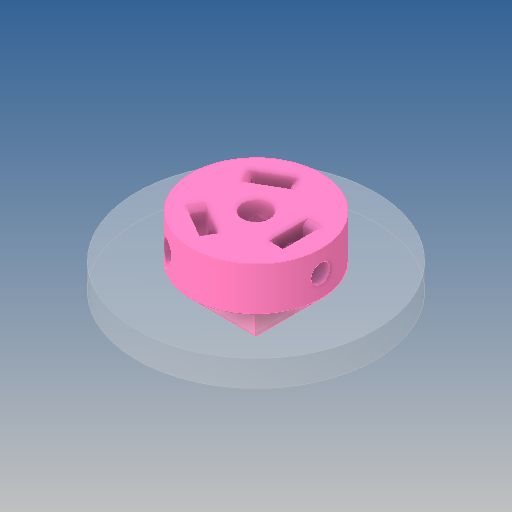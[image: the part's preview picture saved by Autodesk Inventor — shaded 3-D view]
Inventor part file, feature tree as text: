
AUTODESK INVENTOR PART (.ipt)
format: ipt  version: 2017 (Build 210142000, 142)  size: 262,656 bytes
history: native  units: mm
features: extrude x5, other x4, sketch x3, chamfer x2, pattern_circular x1, projected_geometry x1
ambient origin geometry x8: Origin, YZ Plane, XZ Plane, XY Plane, X Axis, Y Axis, Z Axis, Center Point
bodies: Body1 (feature_tree), Body2 (feature_tree)
feature tree (16):
  other  "Sólido1"
  extrude  "Extrusión1"  Depth=11.85mm
  sketch  "Boceto2"  dims[d3=6.576542mm d4=3.3mm]
  extrude  "Extrusión2"  Depth=3.3mm
  extrude  "Extrusión3"  Depth=2.0mm
  sketch  "Boceto3"  dims[d5=10.0mm d6=0.0mm d7=4.2mm d8=120.0deg d9=3.7mm d10=16.0mm d11=0.0mm d12=4.0mm d13=0.0mm d14=8.0mm d15=0.0mm d16=30.0mm d18=360.0deg d20=30.0mm d21=360.0deg d23=1.0mm d24=2.0mm d25=45.0deg d26=30.0mm d27=4.275mm d28=4.275mm d32=16.0mm d33=55.0mm d34=6.0mm d35=0.0mm d36=1.0mm d37=2.0mm d38=45.0deg]
  extrude  "Extrusión4"  TaperAngle=120.0deg  [1 undecoded]
  pattern_circular  "Patrón circular1"  [2 undecoded]
  chamfer  "Chaflán1"  Distance=16.0mm
  extrude  "Extrusión5"  Depth=2.0mm TaperAngle=0.0deg
  chamfer  "Chaflán3"  Distance=8.0mm
  other  "Dientes de engranaje recto4"
  sketch  "Boceto1"  dims[d0=6.3mm d2=11.85mm]
  projected_geometry  "Contorno proyectado1"
  other  "Sólido2"
  other  "Engranaje recto1"
note: 3 required parameter values undecoded (feature->parameter linkage not recoverable at this tier; creation-order binding heuristic only, values carry confidence <= 0.55)
